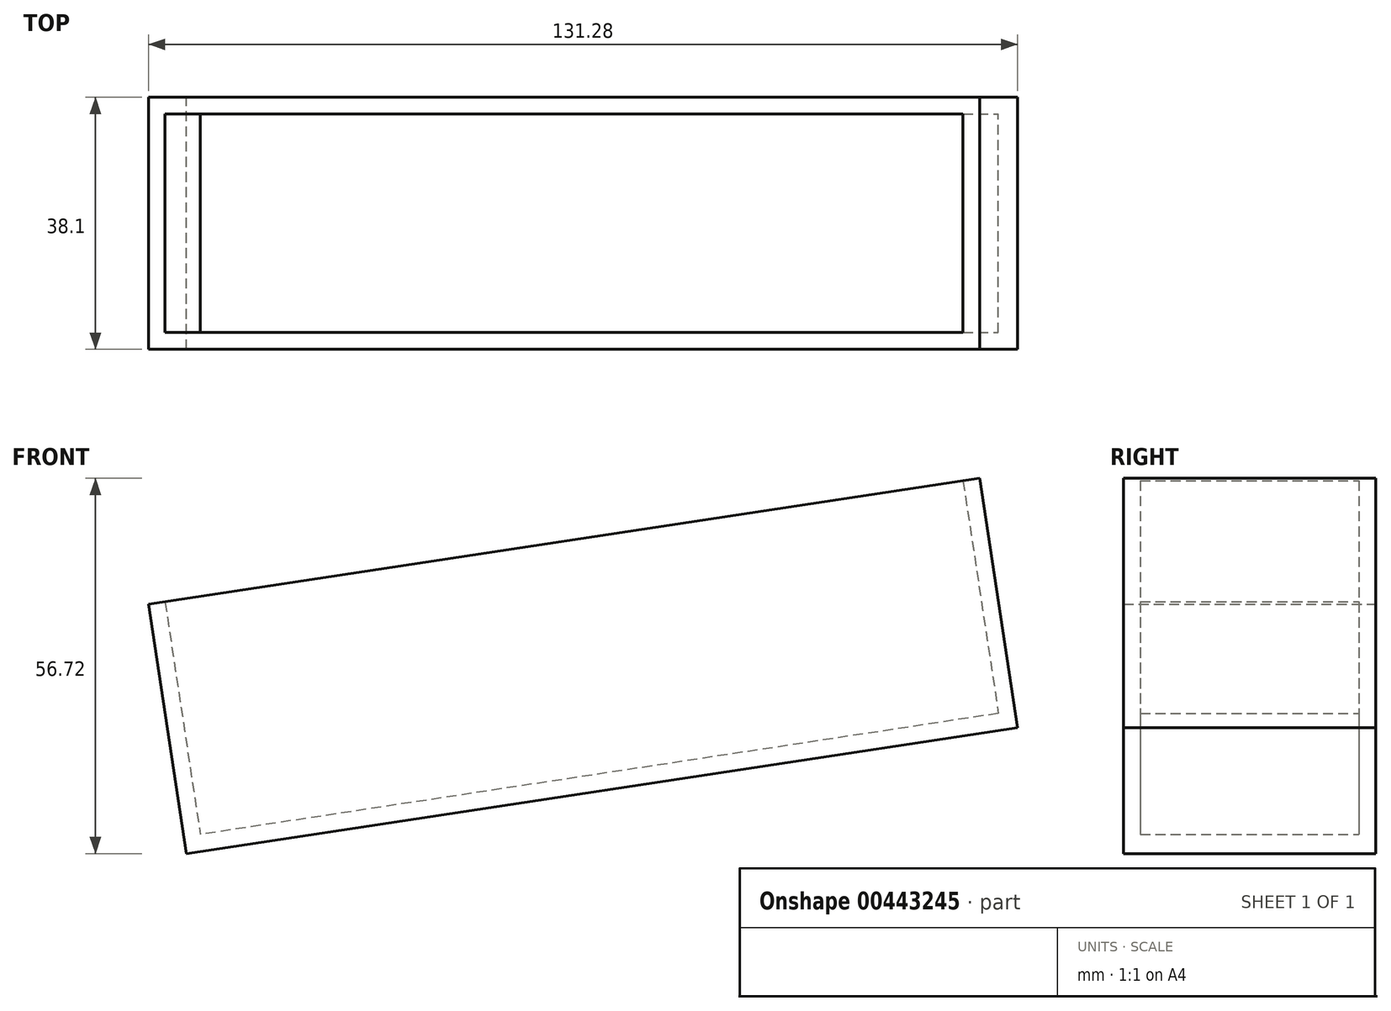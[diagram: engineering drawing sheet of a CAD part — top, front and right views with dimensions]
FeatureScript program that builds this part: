
annotation { "Feature Type Name" : "Feature", "Feature Type Description" : "" }
export const myFeature = defineFeature(function(context is Context, id is Id, definition is map)
    precondition{}
    {
        {
            var Q0;
            Q0=qCreatedBy(makeId("Front.planeOp"),FACE);
            var sketch = newSketch(context, id + "F0", { "sketchPlane" : qUnion([Q0])});
            skLineSegment(sketch, "E0", {"start": v(-50.8, 0) * mm, "end": v(74.76, 19.05) * mm});
            skLineSegment(sketch, "E1", {"start": v(74.76, 19.05) * mm, "end": v(69.05, 56.72) * mm});
            skLineSegment(sketch, "E2", {"start": v(69.05, 56.72) * mm, "end": v(-56.52, 37.67) * mm});
            skLineSegment(sketch, "E3", {"start": v(-56.52, 37.67) * mm, "end": v(-50.8, 0) * mm});
            skLineSegment(sketch, "E4", {"start": v(-54, 38.05) * mm, "end": v(-48.67, 2.9) * mm});
            skLineSegment(sketch, "E5", {"start": v(-48.67, 2.9) * mm, "end": v(71.87, 21.18) * mm});
            skLineSegment(sketch, "E6", {"start": v(71.87, 21.18) * mm, "end": v(66.54, 56.34) * mm});
            skSolve(sketch);
        }
        {
            var Q0;
            Q0=makeQuery(id+"F0.imprint","IMPRINT",FACE,{"disambiguationData":[TD([[makeQuery(id+"F0.imprint","IMPRINT",EDGE,{"derivedFrom":sQuery(id+"F0.wireOp",EDGE,"E0")}),1.0]])]});
            extrude(context, id + "F1", {"entities" : qUnion([Q0]), "depth" : 38.1 * mm, "symmetric" : true});
        }
        {
            var Q0;
            Q0=makeQuery(id+"F1.opExtrude","SWEPT_FACE",FACE,{"disambiguationData":[OSD([sQuery(id+"F0.wireOp",EDGE,"E5")])]});
            var sketch = newSketch(context, id + "F2", { "sketchPlane" : qUnion([Q0])});
            skLineSegment(sketch, "E7", {"start": v(74.23, -16.5) * mm, "end": v(-47.69, -16.51) * mm});
            skLineSegment(sketch, "E8", {"start": v(74.23, 16.51) * mm, "end": v(-47.69, 16.51) * mm});
            skSolve(sketch);
        }
        {
            var Q0;
            {var subQ0=sQuery(id+"F2.wireOp",EDGE,"E8");Q0=makeQuery(id+"F2.imprint","IMPRINT",FACE,{"disambiguationData":[TD([[makeQuery(id+"F2.imprint","IMPRINT",EDGE,{"derivedFrom":subQ0}),-1.0]])]});}
            var Q1;
            {var subQ0=sQuery(id+"F2.wireOp",EDGE,"E7");Q1=makeQuery(id+"F2.imprint","IMPRINT",FACE,{"disambiguationData":[TD([[makeQuery(id+"F2.imprint","IMPRINT",EDGE,{"derivedFrom":subQ0}),1.0]])]});}
            extrude(context, id + "F3", {"entities" : qUnion([Q0, Q1]), "operationType" : NewBodyOperationType.ADD, "depth" : 35.56 * mm});
        }
    });
